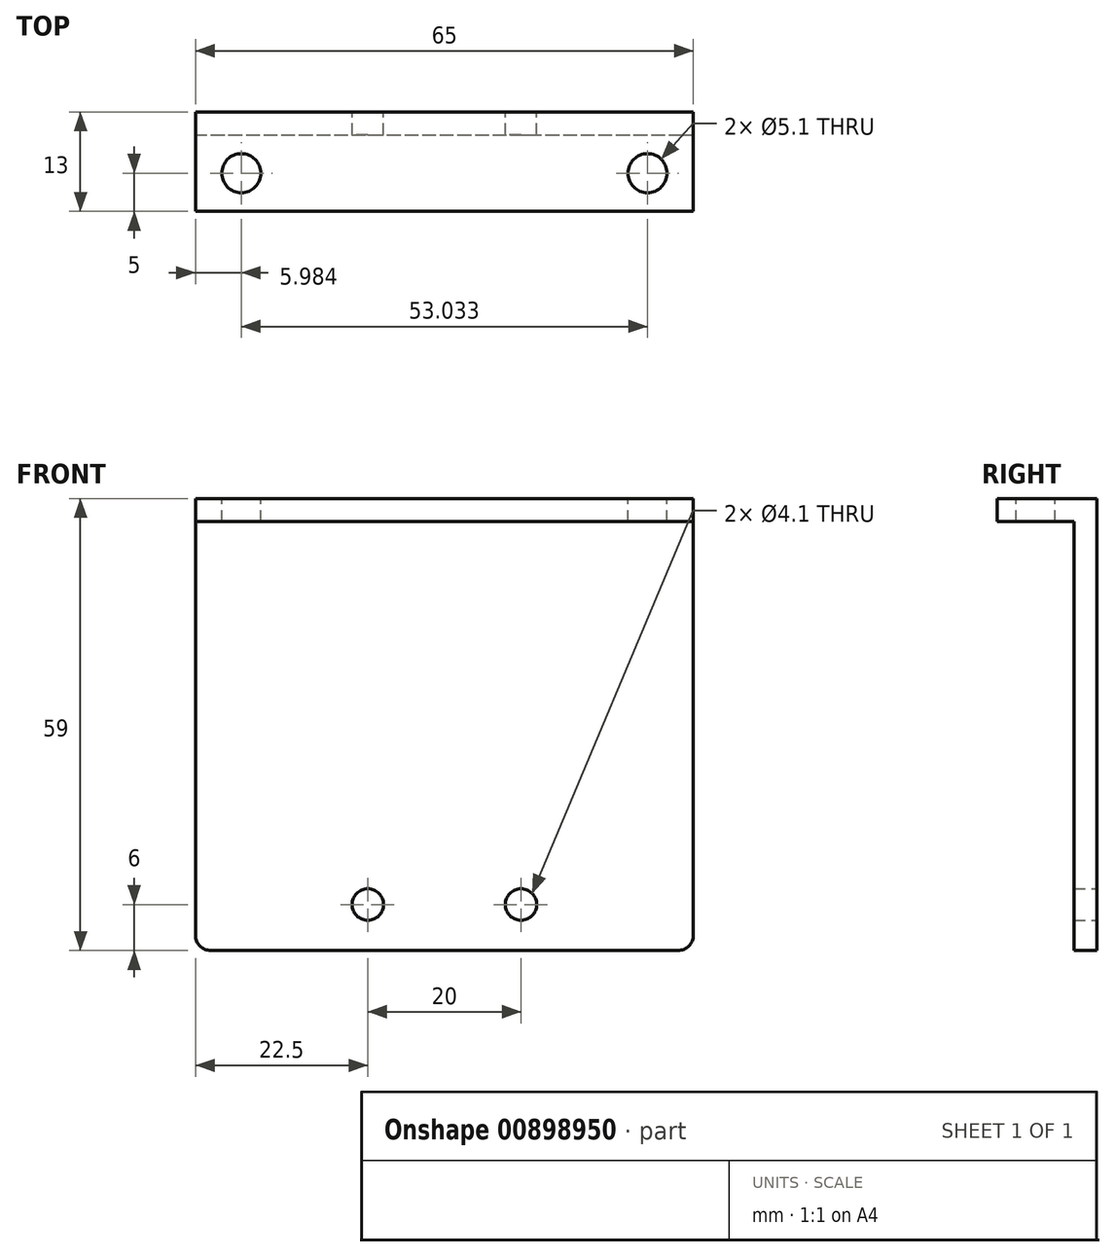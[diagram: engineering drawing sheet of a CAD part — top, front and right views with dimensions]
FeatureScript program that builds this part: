
annotation { "Feature Type Name" : "Feature", "Feature Type Description" : "" }
export const myFeature = defineFeature(function(context is Context, id is Id, definition is map)
    precondition{}
    {
        {
            var Q0;
            Q0=qCreatedBy(makeId("Front.planeOp"),FACE);
            var sketch = newSketch(context, id + "F0", { "sketchPlane" : qUnion([Q0])});
            skLineSegment(sketch, "E0.bottom", {"start": v(0, 0) * mm, "end": v(65, 0) * mm});
            skLineSegment(sketch, "E0.top", {"start": v(0, -59) * mm, "end": v(65, -59) * mm});
            skLineSegment(sketch, "E0.left", {"start": v(0, 0) * mm, "end": v(0, -59) * mm});
            skLineSegment(sketch, "E0.right", {"start": v(65, 0) * mm, "end": v(65, -59) * mm});
            skSolve(sketch);
        }
        {
            var Q0;
            Q0 = qSketchRegion(id + "F0", true);
            extrude(context, id + "F1", {"entities" : qUnion([Q0]), "depth" : 3 * mm, "offsetDistance" : 25 * mm});
        }
        {
            var Q0;
            Q0=makeQuery(id+"F1.opExtrude","CAP_FACE",FACE,{"disambiguationData":[OSD([sQuery(id+"F0.wireOp",EDGE,"E0.bottom"),sQuery(id+"F0.wireOp",EDGE,"E0.top"),sQuery(id+"F0.wireOp",EDGE,"E0.left"),sQuery(id+"F0.wireOp",EDGE,"E0.right")])],"isStart":false});
            var sketch = newSketch(context, id + "F2", { "sketchPlane" : qUnion([Q0])});
            skLineSegment(sketch, "E1.bottom", {"start": v(0, 0) * mm, "end": v(65, 0) * mm});
            skLineSegment(sketch, "E1.top", {"start": v(0, -3) * mm, "end": v(65, -3) * mm});
            skLineSegment(sketch, "E1.left", {"start": v(0, 0) * mm, "end": v(0, -3) * mm});
            skLineSegment(sketch, "E1.right", {"start": v(65, 0) * mm, "end": v(65, -3) * mm});
            skSolve(sketch);
        }
        {
            var Q0;
            Q0 = qSketchRegion(id + "F2", true);
            extrude(context, id + "F3", {"entities" : qUnion([Q0]), "operationType" : NewBodyOperationType.ADD, "depth" : 10 * mm, "offsetDistance" : 25 * mm});
        }
        {
            var Q0;
            Q0=makeQuery(id+"F3.boolean.opBoolean","MERGE",FACE,{"derivedFrom":[makeQuery(id+"F1.opExtrude","SWEPT_FACE",FACE,{"disambiguationData":[OSD([sQuery(id+"F0.wireOp",EDGE,"E0.bottom")])]}),makeQuery(id+"F3.opExtrude","SWEPT_FACE",FACE,{"disambiguationData":[OSD([sQuery(id+"F2.wireOp",EDGE,"E1.bottom")])]})]});
            var sketch = newSketch(context, id + "F4", { "sketchPlane" : qUnion([Q0])});
            skCircle(sketch, "E2", {"center": v(59.02, -8) * mm, "radius": 2.55 * mm});
            skCircle(sketch, "E3", {"center": v(5.98, -8) * mm, "radius": 2.55 * mm});
            skSolve(sketch);
        }
        {
            var Q0;
            Q0 = qSketchRegion(id + "F4", true);
            extrude(context, id + "F5", {"entities" : qUnion([Q0]), "operationType" : NewBodyOperationType.REMOVE, "oppositeDirection" : true, "depth" : 25 * mm, "offsetDistance" : 25 * mm});
        }
        {
            var Q0;
            Q0=makeQuery(id+"F1.opExtrude","CAP_FACE",FACE,{"disambiguationData":[OSD([sQuery(id+"F0.wireOp",EDGE,"E0.bottom"),sQuery(id+"F0.wireOp",EDGE,"E0.top"),sQuery(id+"F0.wireOp",EDGE,"E0.left"),sQuery(id+"F0.wireOp",EDGE,"E0.right")])],"isStart":true});
            var sketch = newSketch(context, id + "F6", { "sketchPlane" : qUnion([Q0])});
            skCircle(sketch, "E4", {"center": v(-42.5, -53) * mm, "radius": 2.05 * mm});
            skCircle(sketch, "E5", {"center": v(-22.5, -53) * mm, "radius": 2.05 * mm});
            skSolve(sketch);
        }
        {
            var Q0;
            Q0 = qSketchRegion(id + "F6", true);
            extrude(context, id + "F7", {"entities" : qUnion([Q0]), "operationType" : NewBodyOperationType.REMOVE, "oppositeDirection" : true, "depth" : 25 * mm, "offsetDistance" : 25 * mm});
        }
        {
            var Q0;
            Q0=makeQuery(id+"F1.opExtrude","SWEPT_EDGE",EDGE,{"disambiguationData":[OSD([sQuery(id+"F0.wireOp",EDGE,"E0.top"),sQuery(id+"F0.wireOp",EDGE,"E0.right")])]});
            var Q1;
            Q1=makeQuery(id+"F1.opExtrude","SWEPT_EDGE",EDGE,{"disambiguationData":[OSD([sQuery(id+"F0.wireOp",EDGE,"E0.top"),sQuery(id+"F0.wireOp",EDGE,"E0.left")])]});
            fillet(context, id + "F8", {"entities" : qUnion([Q0, Q1]), "radius" : 2 * mm, "tangentPropagation" : true, "allowEdgeOverflow" : false});
        }
    });
